# Revit family: 3097942 Lighting Fixture_Sylvania_Nephos LED_Ceiling Pendant
name_source: partatom
category: Lighting Fixtures
revit_build: Autodesk Revit 2017 (Build: 20190507_1515(x64)
units: mm (PartAtom-declared; Revit-internal decimal feet)

## family parameters
Cut with Voids When Loaded = No
Host = Face
Light Source = Yes
OmniClass Number = 23.80.70.11.17
OmniClass Title = Specialized Lighting by Location or Use
Part Type = Normal
Room Calculation Point = No
Round Connector Dimension = Use Diameter
Shared = No

## types (1)
- NEPHOS 600 LED V2 GLOSS BLACK NW EB
    Apparent Load = 24 VA
    Assembly Code = D5020200
    Body Material = Aluminium_Sylvania_Nephos_Black
    CRI ( Ra ) = 85
    Catalog Number = 3097942 NEPHOS 600 LED V2 GLOSS BLACK NW EB
    Color Filter = 16777215
    Default Elevation = 0 mm  [stored 0 ft]
    Description = High-end and decorative LED pendant with a contemporary curved design. Available in gloss black and gloss white colour finishes to suit either a high brightness reception, or an ambient lounge space. Diffused (direct) light provides a soft and ambient lighting effect. Perfect for hospitality and residential applications; can be used in restaurants, bars, reception areas or lounge spaces. Aluminium housing material. 600mm diameter. Delivers up to 1340lm (4000K luminaire lumen output). Available in 3000K and 4000K colour temperatures. DALI dimmable options. 25W. LED technology provides energy efficient solution and reduced maintenance costs. 50,000 hour life. Adjustable 2000mm suspension cable
    Diameter = 600 mm
    Diffuser Material = Polycarbonate_Sylvania_Nephos_Opal
    Diffuser Radius = 295 mm  [stored 0.967848 ft]
    Dimming Lamp Color Temperature Shift = <None>
    Drive Current = 700mA
    Electrical Protection = Class I
    Emit Shape Visible in Rendering = No
    Emit from Circle Diameter = 590 mm  [stored 1.9357 ft]
    Glow Wire Test = 650 °C
    Height = 200 mm  [stored 0.656168 ft]
    IP Rating = IP20
    LOR = 100%
    Lamp = Integrated LED
    Life = 50 000h
    Manufacturer = Feilo Sylvania
    Model = NEPHOS 600 LED V2 GLOSS BLACK NW EB
    Mounting Height = 2000 mm  [stored 6.56168 ft]
    Mounting Material = Steel_Sylvania_Nephos_Silver
    Mounting Radius = 62 mm  [stored 0.203412 ft]
    Photometric Web File = 3097942_NEPHOS600LEDV2GLOSSBLACKNWEB-209097.ies
    Product Family = NEPHOS
    Product Page URL = http://www.sylvania-lighting.com
    Radius = 300 mm
    Rod Length = 1743 mm  [stored 5.7185 ft]
    Tilt Angle = -90°
    URL = http://www.sylvania-lighting.com
    Voltage = 230 V
    Voltage Comments = UNV (Universal Voltage; 220-240 Volt)
    Weight = 5 kg

note: [stored X ft] marks values corroborated as IEEE doubles in the binary element streams (Revit-internal decimal feet)

## geometry (parser evidence)
native form markers: Blend x6, Sweep x5
no freeform markers — native parametric forms only
